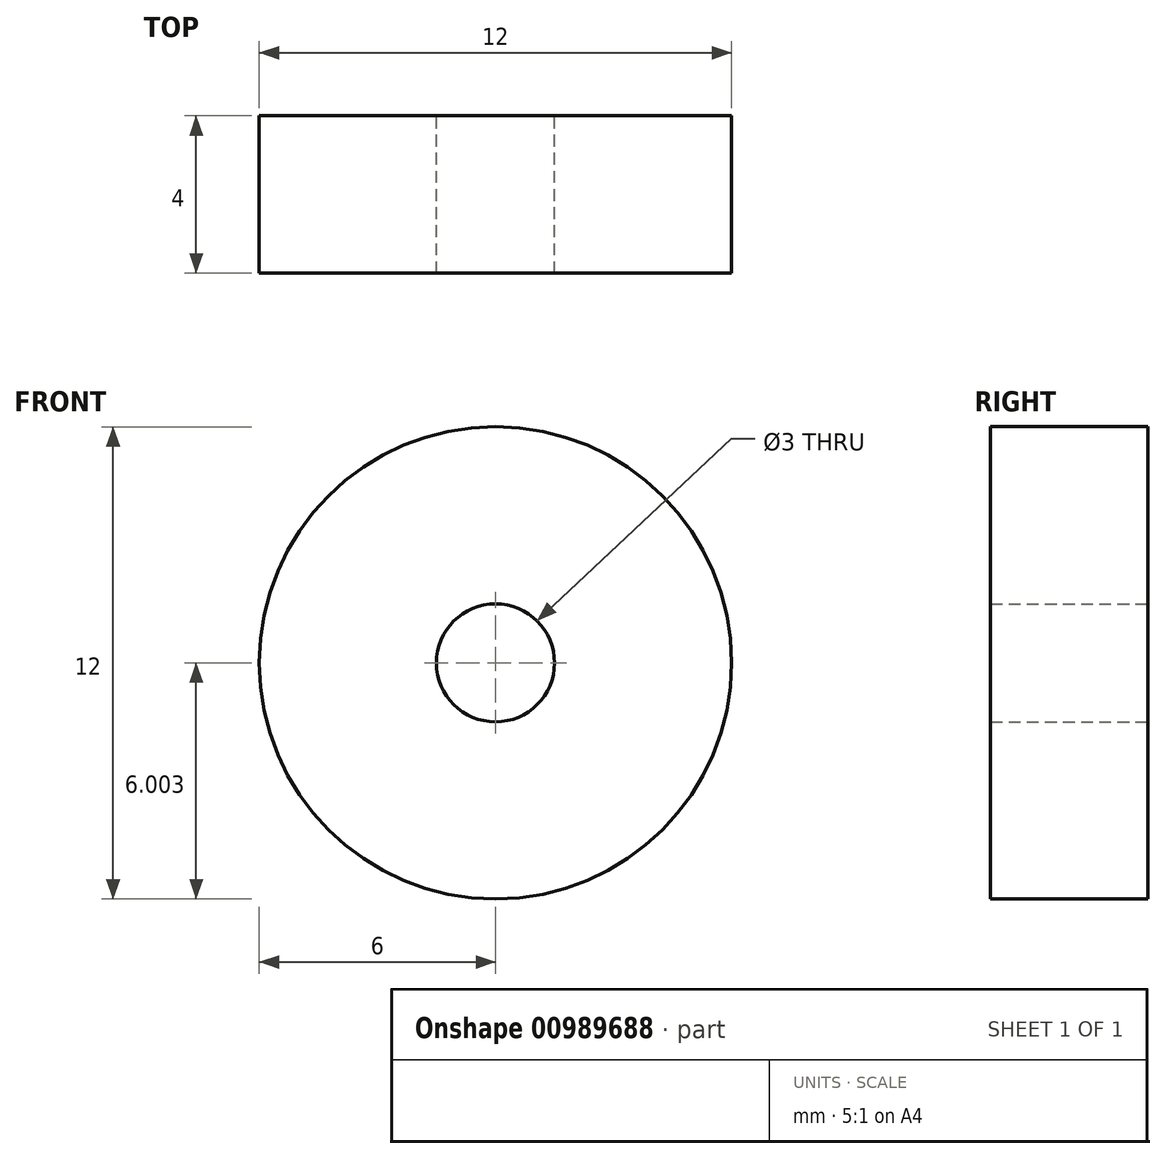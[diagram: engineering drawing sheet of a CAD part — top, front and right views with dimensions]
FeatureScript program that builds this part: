
annotation { "Feature Type Name" : "Feature", "Feature Type Description" : "" }
export const myFeature = defineFeature(function(context is Context, id is Id, definition is map)
    precondition{}
    {
        {
            var Q0;
            Q0=qCreatedBy(makeId("Front.planeOp"),FACE);
            var sketch = newSketch(context, id + "F0", { "sketchPlane" : qUnion([Q0])});
            skCircle(sketch, "E0", {"center": v(-51.62, 42.01) * mm, "radius": 6 * mm});
            skCircle(sketch, "E1", {"center": v(-51.62, 42.01) * mm, "radius": 1.5 * mm});
            skSolve(sketch);
        }
        {
            var Q0;
            Q0=makeQuery(id+"F0.imprint","IMPRINT",FACE,{"disambiguationData":[TD([[makeQuery(id+"F0.imprint","IMPRINT",EDGE,{"derivedFrom":sQuery(id+"F0.wireOp",EDGE,"E0")}),1.0]])]});
            extrude(context, id + "F1", {"entities" : qUnion([Q0]), "depth" : 4 * mm, "offsetDistance" : 25.4 * mm});
        }
    });
